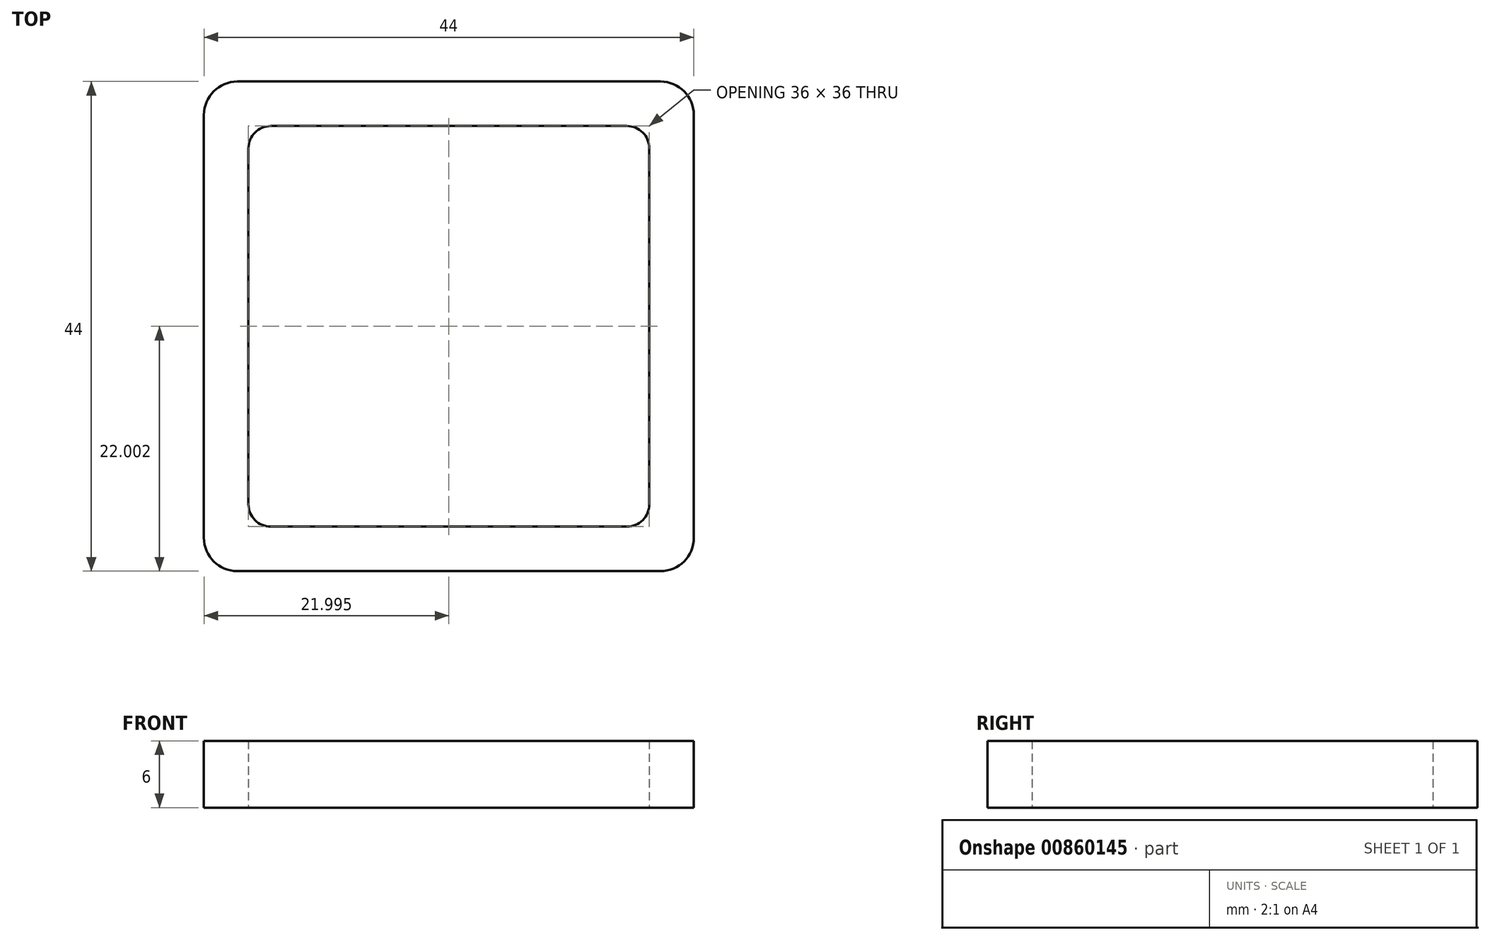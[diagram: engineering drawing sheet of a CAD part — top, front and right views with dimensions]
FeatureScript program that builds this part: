
annotation { "Feature Type Name" : "Feature", "Feature Type Description" : "" }
export const myFeature = defineFeature(function(context is Context, id is Id, definition is map)
    precondition{}
    {
        {
            var Q0;
            Q0=qCreatedBy(makeId("Top.planeOp"),FACE);
            var sketch = newSketch(context, id + "F0", { "sketchPlane" : qUnion([Q0])});
            skLineSegment(sketch, "E0.bottom", {"start": v(-15.92, 20.08) * mm, "end": v(22.08, 20.08) * mm});
            skLineSegment(sketch, "E0.top", {"start": v(-15.92, -23.92) * mm, "end": v(22.08, -23.92) * mm});
            skLineSegment(sketch, "E0.left", {"start": v(-18.92, 17.08) * mm, "end": v(-18.92, -20.92) * mm});
            skLineSegment(sketch, "E0.right", {"start": v(25.08, 17.08) * mm, "end": v(25.08, -20.92) * mm});
            skLineSegment(sketch, "E1.bottom", {"start": v(-12.92, 16.08) * mm, "end": v(19.08, 16.08) * mm});
            skLineSegment(sketch, "E1.top", {"start": v(-12.92, -19.92) * mm, "end": v(19.08, -19.92) * mm});
            skLineSegment(sketch, "E1.left", {"start": v(-14.92, 14.08) * mm, "end": v(-14.92, -17.92) * mm});
            skLineSegment(sketch, "E1.right", {"start": v(21.08, 14.08) * mm, "end": v(21.08, -17.92) * mm});
            skPoint(sketch, "E2.visualSharp", {"position": v(-18.92, 20.08) * mm});
            skArc(sketch, "E2.filletArc", {"start": v(-15.92, 20.08) * mm, "mid": v(-18.05, 19.2) * mm, "end": v(-18.92, 17.08) * mm});
            skPoint(sketch, "E3.visualSharp", {"position": v(25.08, 20.08) * mm});
            skArc(sketch, "E3.filletArc", {"start": v(25.08, 17.08) * mm, "mid": v(24.2, 19.2) * mm, "end": v(22.08, 20.08) * mm});
            skPoint(sketch, "E4.visualSharp", {"position": v(21.08, 16.08) * mm});
            skArc(sketch, "E4.filletArc", {"start": v(21.08, 14.08) * mm, "mid": v(20.49, 15.5) * mm, "end": v(19.08, 16.08) * mm});
            skPoint(sketch, "E5.visualSharp", {"position": v(-14.92, 16.08) * mm});
            skArc(sketch, "E5.filletArc", {"start": v(-12.92, 16.08) * mm, "mid": v(-14.34, 15.5) * mm, "end": v(-14.92, 14.08) * mm});
            skPoint(sketch, "E6.visualSharp", {"position": v(-18.92, -23.92) * mm});
            skArc(sketch, "E6.filletArc", {"start": v(-18.92, -20.92) * mm, "mid": v(-18.05, -23.04) * mm, "end": v(-15.92, -23.92) * mm});
            skPoint(sketch, "E7.visualSharp", {"position": v(25.08, -23.92) * mm});
            skArc(sketch, "E7.filletArc", {"start": v(22.08, -23.92) * mm, "mid": v(24.2, -23.04) * mm, "end": v(25.08, -20.92) * mm});
            skPoint(sketch, "E8.visualSharp", {"position": v(21.08, -19.92) * mm});
            skArc(sketch, "E8.filletArc", {"start": v(19.08, -19.92) * mm, "mid": v(20.49, -19.33) * mm, "end": v(21.08, -17.92) * mm});
            skPoint(sketch, "E9.visualSharp", {"position": v(-14.92, -19.92) * mm});
            skArc(sketch, "E9.filletArc", {"start": v(-14.92, -17.92) * mm, "mid": v(-14.34, -19.33) * mm, "end": v(-12.92, -19.92) * mm});
            skSolve(sketch);
        }
        {
            var Q0;
            Q0 = qSketchRegion(id + "F0", true);
            extrude(context, id + "F1", {"entities" : qUnion([Q0]), "depth" : 6 * mm, "offsetDistance" : 25 * mm});
        }
    });
